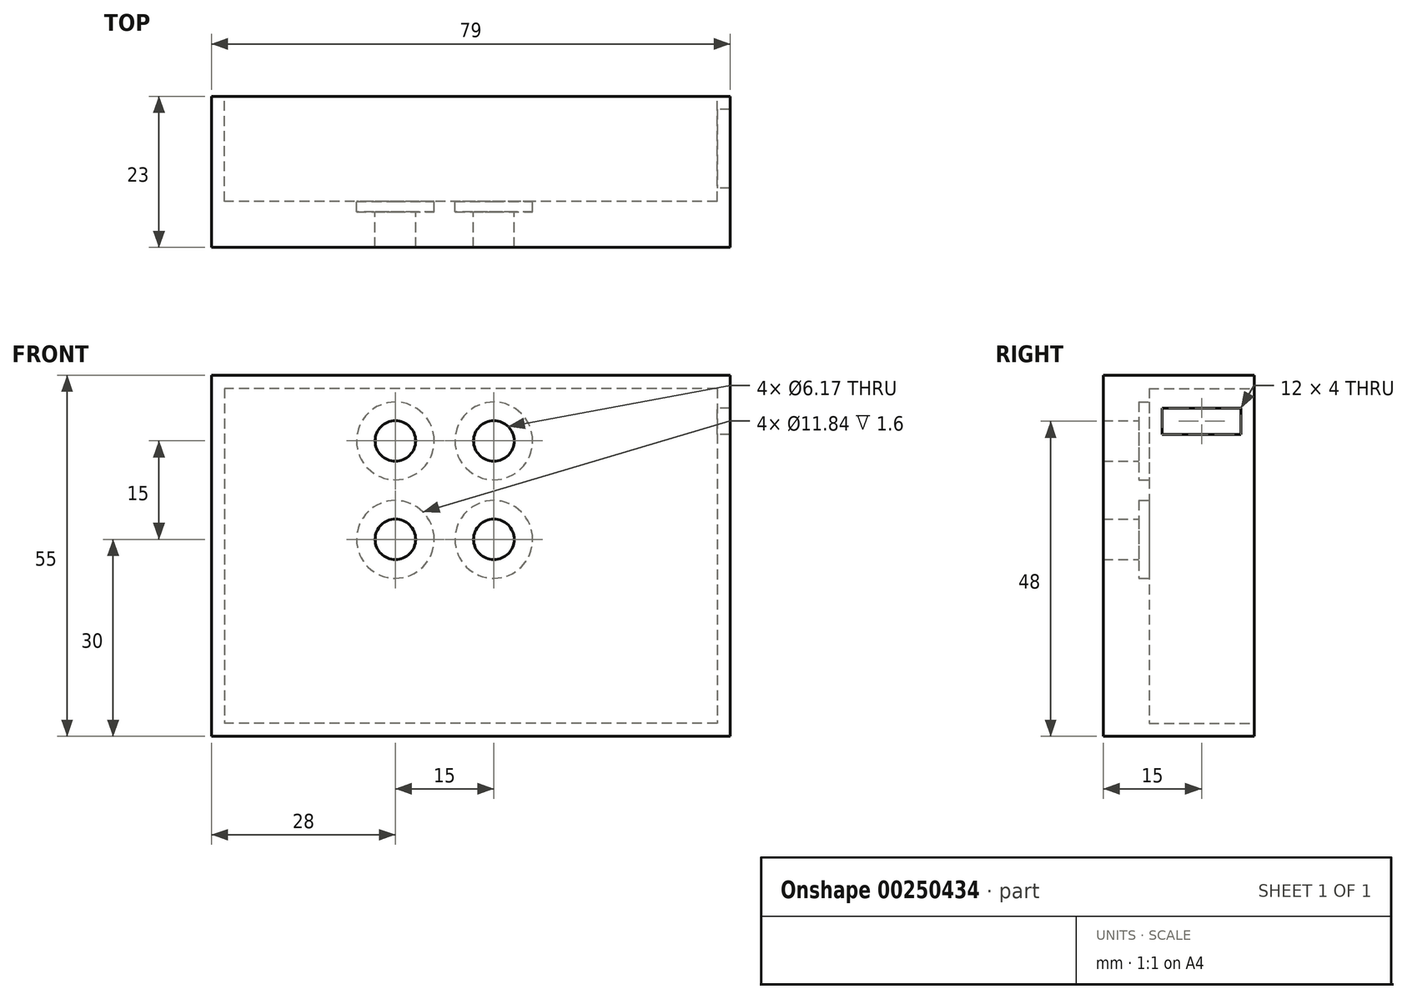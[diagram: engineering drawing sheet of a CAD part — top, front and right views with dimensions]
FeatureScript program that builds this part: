
annotation { "Feature Type Name" : "Feature", "Feature Type Description" : "" }
export const myFeature = defineFeature(function(context is Context, id is Id, definition is map)
    precondition{}
    {
        {
            var Q0;
            Q0=qCreatedBy(makeId("Front.planeOp"),FACE);
            var sketch = newSketch(context, id + "F0", { "sketchPlane" : qUnion([Q0])});
            skLineSegment(sketch, "E0.bottom", {"start": v(39.5, -27.5) * mm, "end": v(-39.5, -27.5) * mm});
            skLineSegment(sketch, "E0.top", {"start": v(39.5, 27.5) * mm, "end": v(-39.5, 27.5) * mm});
            skLineSegment(sketch, "E0.left", {"start": v(39.5, -27.5) * mm, "end": v(39.5, 27.5) * mm});
            skLineSegment(sketch, "E0.right", {"start": v(-39.5, -27.5) * mm, "end": v(-39.5, 27.5) * mm});
            skPoint(sketch, "E0.middle", {"position": v(0, 0) * mm});
            skSolve(sketch);
        }
        {
            var Q0;
            Q0 = qSketchRegion(id + "F0", true);
            extrude(context, id + "F1", {"entities" : qUnion([Q0]), "depth" : 23 * mm});
        }
        {
            var Q0;
            Q0=makeQuery(id+"F1.opExtrude","CAP_FACE",FACE,{"disambiguationData":[OSD([sQuery(id+"F0.wireOp",EDGE,"E0.bottom"),sQuery(id+"F0.wireOp",EDGE,"E0.top"),sQuery(id+"F0.wireOp",EDGE,"E0.left"),sQuery(id+"F0.wireOp",EDGE,"E0.right")])],"isStart":true});
            var sketch = newSketch(context, id + "F2", { "sketchPlane" : qUnion([Q0])});
            skLineSegment(sketch, "E1.0", {"start": v(-39.5, 27.5) * mm, "end": v(39.5, 27.5) * mm, "construction": true});
            skLineSegment(sketch, "E1.1", {"start": v(-39.5, -27.5) * mm, "end": v(-39.5, 27.5) * mm, "construction": true});
            skLineSegment(sketch, "E1.2", {"start": v(-39.5, -27.5) * mm, "end": v(39.5, -27.5) * mm, "construction": true});
            skLineSegment(sketch, "E1.3", {"start": v(39.5, -27.5) * mm, "end": v(39.5, 27.5) * mm, "construction": true});
            skLineSegment(sketch, "E2.bottom", {"start": v(-37.5, 25.5) * mm, "end": v(37.5, 25.5) * mm});
            skLineSegment(sketch, "E2.top", {"start": v(-37.5, -25.5) * mm, "end": v(37.5, -25.5) * mm});
            skLineSegment(sketch, "E2.left", {"start": v(-37.5, 25.5) * mm, "end": v(-37.5, -25.5) * mm});
            skLineSegment(sketch, "E2.right", {"start": v(37.5, 25.5) * mm, "end": v(37.5, -25.5) * mm});
            skSolve(sketch);
        }
        {
            var Q0;
            Q0 = qSketchRegion(id + "F2", true);
            extrude(context, id + "F3", {"entities" : qUnion([Q0]), "operationType" : NewBodyOperationType.REMOVE, "oppositeDirection" : true, "depth" : (21 - 5) * mm});
        }
        {
            var Q0;
            Q0=qCreatedBy(makeId("Right.planeOp"),FACE);
            var sketch = newSketch(context, id + "F4", { "sketchPlane" : qUnion([Q0])});
            skLineSegment(sketch, "E3.bottom", {"start": v(-14, 22.5) * mm, "end": v(-2, 22.5) * mm});
            skLineSegment(sketch, "E3.top", {"start": v(-14, 18.5) * mm, "end": v(-2, 18.5) * mm});
            skLineSegment(sketch, "E3.left", {"start": v(-14, 22.5) * mm, "end": v(-14, 18.5) * mm});
            skLineSegment(sketch, "E3.right", {"start": v(-2, 22.5) * mm, "end": v(-2, 18.5) * mm});
            skLineSegment(sketch, "E4.0.0", {"start": v(-16, 25.5) * mm, "end": v(-16, -25.5) * mm, "construction": true});
            skLineSegment(sketch, "E4.0.2", {"start": v(-16, -25.5) * mm, "end": v(-16, 25.5) * mm, "construction": true});
            skSolve(sketch);
        }
        {
            var Q0;
            Q0 = qSketchRegion(id + "F4", true);
            extrude(context, id + "F5", {"entities" : qUnion([Q0]), "operationType" : NewBodyOperationType.REMOVE, "depth" : 55 * mm});
        }
        {
            var Q0;
            Q0=qCreatedBy(makeId("Front.planeOp"),FACE);
            var sketch = newSketch(context, id + "F6", { "sketchPlane" : qUnion([Q0])});
            skCircle(sketch, "E5", {"center": v(-11.5, 17.5) * mm, "radius": 3.09 * mm});
            skCircle(sketch, "E6", {"center": v(-11.5, 2.5) * mm, "radius": 3.09 * mm});
            skCircle(sketch, "E7", {"center": v(3.5, 2.5) * mm, "radius": 3.09 * mm});
            skCircle(sketch, "E8", {"center": v(3.5, 17.5) * mm, "radius": 3.09 * mm});
            skSolve(sketch);
        }
        {
            var Q0;
            Q0 = qSketchRegion(id + "F6", true);
            extrude(context, id + "F7", {"entities" : qUnion([Q0]), "operationType" : NewBodyOperationType.REMOVE, "depth" : 25 * mm});
        }
        {
            var Q0;
            Q0=makeQuery(id+"F3.boolean.opBoolean","COPY",FACE,{"derivedFrom":makeQuery(id+"F3.opExtrude","CAP_FACE",FACE,{"disambiguationData":[OSD([sQuery(id+"F2.wireOp",EDGE,"E2.bottom"),sQuery(id+"F2.wireOp",EDGE,"E2.top"),sQuery(id+"F2.wireOp",EDGE,"E2.left"),sQuery(id+"F2.wireOp",EDGE,"E2.right")])],"isStart":false})});
            var sketch = newSketch(context, id + "F8", { "sketchPlane" : qUnion([Q0])});
            skCircle(sketch, "E9", {"center": v(-3.5, 17.5) * mm, "radius": 5.92 * mm});
            skCircle(sketch, "E10", {"center": v(-3.5, 2.5) * mm, "radius": 5.92 * mm});
            skCircle(sketch, "E11", {"center": v(11.5, 2.5) * mm, "radius": 5.92 * mm});
            skCircle(sketch, "E12", {"center": v(11.5, 17.5) * mm, "radius": 5.92 * mm});
            skSolve(sketch);
        }
        {
            var Q0;
            Q0 = qSketchRegion(id + "F8", true);
            extrude(context, id + "F9", {"entities" : qUnion([Q0]), "operationType" : NewBodyOperationType.REMOVE, "oppositeDirection" : true, "depth" : 1.6 * mm});
        }
    });
